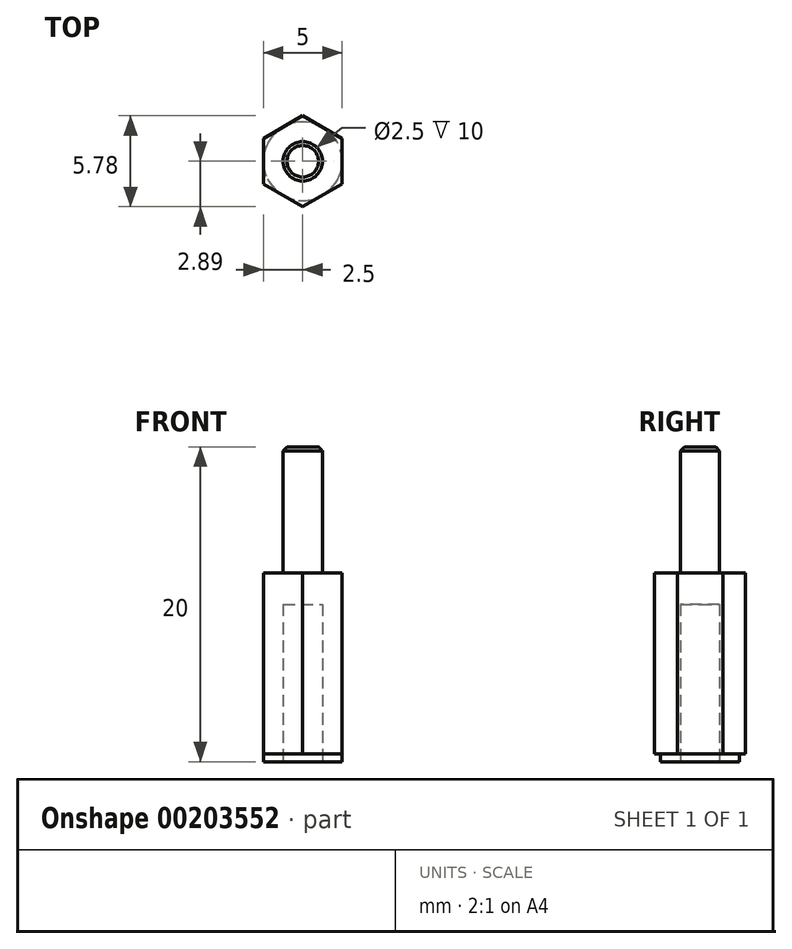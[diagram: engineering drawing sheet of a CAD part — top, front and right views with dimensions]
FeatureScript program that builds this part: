
annotation { "Feature Type Name" : "Feature", "Feature Type Description" : "" }
export const myFeature = defineFeature(function(context is Context, id is Id, definition is map)
    precondition{}
    {
        {
            var Q0;
            Q0=qCreatedBy(makeId("Top.planeOp"),FACE);
            var sketch = newSketch(context, id + "F0", { "sketchPlane" : qUnion([Q0])});
            skCircle(sketch, "E0", {"center": v(0, 0) * mm, "radius": 2.5 * mm});
            skSolve(sketch);
        }
        {
            var Q0;
            Q0=makeQuery(id+"F0.imprint","IMPRINT",FACE,{"disambiguationData":[TD([[makeQuery(id+"F0.imprint","IMPRINT",EDGE,{"derivedFrom":sQuery(id+"F0.wireOp",EDGE,"E0")}),1.0]])]});
            extrude(context, id + "F1", {"entities" : qUnion([Q0]), "depth" : 0.5 * mm});
        }
        {
            var Q0;
            Q0=makeQuery(id+"F1.opExtrude","CAP_FACE",FACE,{"disambiguationData":[OSD([sQuery(id+"F0.wireOp",EDGE,"E0")])],"isStart":false});
            var sketch = newSketch(context, id + "F2", { "sketchPlane" : qUnion([Q0])});
            skCircle(sketch, "E1.cCircle", {"center": v(0, 0) * mm, "radius": 2.5 * mm, "construction": true});
            skLineSegment(sketch, "E1.0", {"start": v(2.5, 1.44) * mm, "end": v(2.5, -1.44) * mm});
            skLineSegment(sketch, "E1.1", {"start": v(2.5, -1.44) * mm, "end": v(0, -2.89) * mm});
            skLineSegment(sketch, "E1.2", {"start": v(0, -2.89) * mm, "end": v(-2.5, -1.44) * mm});
            skLineSegment(sketch, "E1.3", {"start": v(-2.5, -1.44) * mm, "end": v(-2.5, 1.44) * mm});
            skLineSegment(sketch, "E1.4", {"start": v(-2.5, 1.44) * mm, "end": v(0, 2.89) * mm});
            skLineSegment(sketch, "E1.5", {"start": v(0, 2.89) * mm, "end": v(2.5, 1.44) * mm});
            skPoint(sketch, "E1.0.midPoint", {"position": v(2.5, 0) * mm});
            skSolve(sketch);
        }
        {
            var Q0;
            {var subQ0=sQuery(id+"F2.wireOp",EDGE,"E1.5");var subQ1=sQuery(id+"F2.wireOp",EDGE,"E1.0");var subQ2=makeQuery(id+"F2.imprint","INTERSECT",VERTEX,{"derivedFrom":[subQ1,subQ0]});Q0=makeQuery(id+"F2.imprint","IMPRINT",FACE,{"disambiguationData":[TD([[makeQuery(id+"F2.imprint","IMPRINT",EDGE,{"disambiguationData":[TD([[subQ2,-1.0]])],"derivedFrom":subQ1}),-1.0]])]});}
            var Q1;
            {var subQ0=sQuery(id+"F2.wireOp",EDGE,"E1.1");var subQ1=sQuery(id+"F2.wireOp",EDGE,"E1.0");var subQ2=makeQuery(id+"F2.imprint","INTERSECT",VERTEX,{"derivedFrom":[subQ1,subQ0]});Q1=makeQuery(id+"F2.imprint","IMPRINT",FACE,{"disambiguationData":[TD([[makeQuery(id+"F2.imprint","IMPRINT",EDGE,{"disambiguationData":[TD([[subQ2,1.0]])],"derivedFrom":subQ1}),-1.0]])]});}
            var Q2;
            {var subQ0=sQuery(id+"F2.wireOp",EDGE,"E1.2");var subQ1=sQuery(id+"F2.wireOp",EDGE,"E1.1");var subQ2=makeQuery(id+"F2.imprint","INTERSECT",VERTEX,{"derivedFrom":[subQ1,subQ0]});Q2=makeQuery(id+"F2.imprint","IMPRINT",FACE,{"disambiguationData":[TD([[makeQuery(id+"F2.imprint","IMPRINT",EDGE,{"disambiguationData":[TD([[subQ2,1.0]])],"derivedFrom":subQ1}),-1.0]])]});}
            var Q3;
            {var subQ0=sQuery(id+"F2.wireOp",EDGE,"E1.3");var subQ1=sQuery(id+"F2.wireOp",EDGE,"E1.2");var subQ2=makeQuery(id+"F2.imprint","INTERSECT",VERTEX,{"derivedFrom":[subQ1,subQ0]});Q3=makeQuery(id+"F2.imprint","IMPRINT",FACE,{"disambiguationData":[TD([[makeQuery(id+"F2.imprint","IMPRINT",EDGE,{"disambiguationData":[TD([[subQ2,1.0]])],"derivedFrom":subQ1}),-1.0]])]});}
            var Q4;
            {var subQ0=sQuery(id+"F2.wireOp",EDGE,"E1.4");var subQ1=sQuery(id+"F2.wireOp",EDGE,"E1.3");var subQ2=makeQuery(id+"F2.imprint","INTERSECT",VERTEX,{"derivedFrom":[subQ1,subQ0]});Q4=makeQuery(id+"F2.imprint","IMPRINT",FACE,{"disambiguationData":[TD([[makeQuery(id+"F2.imprint","IMPRINT",EDGE,{"disambiguationData":[TD([[subQ2,1.0]])],"derivedFrom":subQ1}),-1.0]])]});}
            var Q5;
            {var subQ0=makeQuery(id+"F1.opExtrude","CAP_EDGE",EDGE,{"disambiguationData":[OSD([sQuery(id+"F0.wireOp",EDGE,"E0")])],"isStart":false});var subQ6=makeQuery(id+"F2.imprint","INTERSECT",VERTEX,{"derivedFrom":[subQ0,sQuery(id+"F2.wireOp",EDGE,"E1.0")]});Q5=makeQuery(id+"F2.imprint","IMPRINT",FACE,{"disambiguationData":[TD([[makeQuery(id+"F2.imprint","IMPRINT",EDGE,{"disambiguationData":[TD([[subQ6,1.0]])],"derivedFrom":subQ0}),1.0]])]});}
            var Q6;
            {var subQ0=sQuery(id+"F2.wireOp",EDGE,"E1.5");var subQ1=sQuery(id+"F2.wireOp",EDGE,"E1.4");var subQ2=makeQuery(id+"F2.imprint","INTERSECT",VERTEX,{"derivedFrom":[subQ1,subQ0]});Q6=makeQuery(id+"F2.imprint","IMPRINT",FACE,{"disambiguationData":[TD([[makeQuery(id+"F2.imprint","IMPRINT",EDGE,{"disambiguationData":[TD([[subQ2,1.0]])],"derivedFrom":subQ1}),-1.0]])]});}
            extrude(context, id + "F3", {"entities" : qUnion([Q0, Q1, Q2, Q3, Q4, Q5, Q6]), "operationType" : NewBodyOperationType.ADD, "depth" : 11.5 * mm});
        }
        {
            var Q0;
            Q0=makeQuery(id+"F3.opExtrude","CAP_FACE",FACE,{"disambiguationData":[OSD([sQuery(id+"F2.wireOp",EDGE,"E1.0"),sQuery(id+"F2.wireOp",EDGE,"E1.1"),sQuery(id+"F2.wireOp",EDGE,"E1.2"),sQuery(id+"F2.wireOp",EDGE,"E1.3"),sQuery(id+"F2.wireOp",EDGE,"E1.4"),sQuery(id+"F2.wireOp",EDGE,"E1.5")])],"isStart":false});
            var sketch = newSketch(context, id + "F4", { "sketchPlane" : qUnion([Q0])});
            skCircle(sketch, "E2", {"center": v(0, 0) * mm, "radius": 1.25 * mm});
            skSolve(sketch);
        }
        {
            var Q0;
            Q0=makeQuery(id+"F4.imprint","IMPRINT",FACE,{"disambiguationData":[TD([[makeQuery(id+"F4.imprint","IMPRINT",EDGE,{"derivedFrom":sQuery(id+"F4.wireOp",EDGE,"E2")}),1.0]])]});
            extrude(context, id + "F5", {"entities" : qUnion([Q0]), "operationType" : NewBodyOperationType.ADD, "depth" : 8 * mm});
        }
        {
            var Q0;
            Q0=makeQuery(id+"F5.opExtrude","CAP_EDGE",EDGE,{"disambiguationData":[OSD([sQuery(id+"F4.wireOp",EDGE,"E2")])],"isStart":false});
            chamfer(context, id + "F6", {"entities" : qUnion([Q0]), "width" : 0.25 * mm, "tangentPropagation" : true});
        }
        {
            var Q0;
            Q0=makeQuery(id+"F1.opExtrude","CAP_FACE",FACE,{"disambiguationData":[OSD([sQuery(id+"F0.wireOp",EDGE,"E0")])],"isStart":true});
            var sketch = newSketch(context, id + "F7", { "sketchPlane" : qUnion([Q0])});
            skCircle(sketch, "E3", {"center": v(0, 0) * mm, "radius": 1.25 * mm});
            skSolve(sketch);
        }
        {
            var Q0;
            Q0=makeQuery(id+"F7.imprint","IMPRINT",FACE,{"disambiguationData":[TD([[makeQuery(id+"F7.imprint","IMPRINT",EDGE,{"derivedFrom":sQuery(id+"F7.wireOp",EDGE,"E3")}),1.0]])]});
            extrude(context, id + "F8", {"entities" : qUnion([Q0]), "operationType" : NewBodyOperationType.REMOVE, "oppositeDirection" : true, "depth" : 10 * mm});
        }
    });
